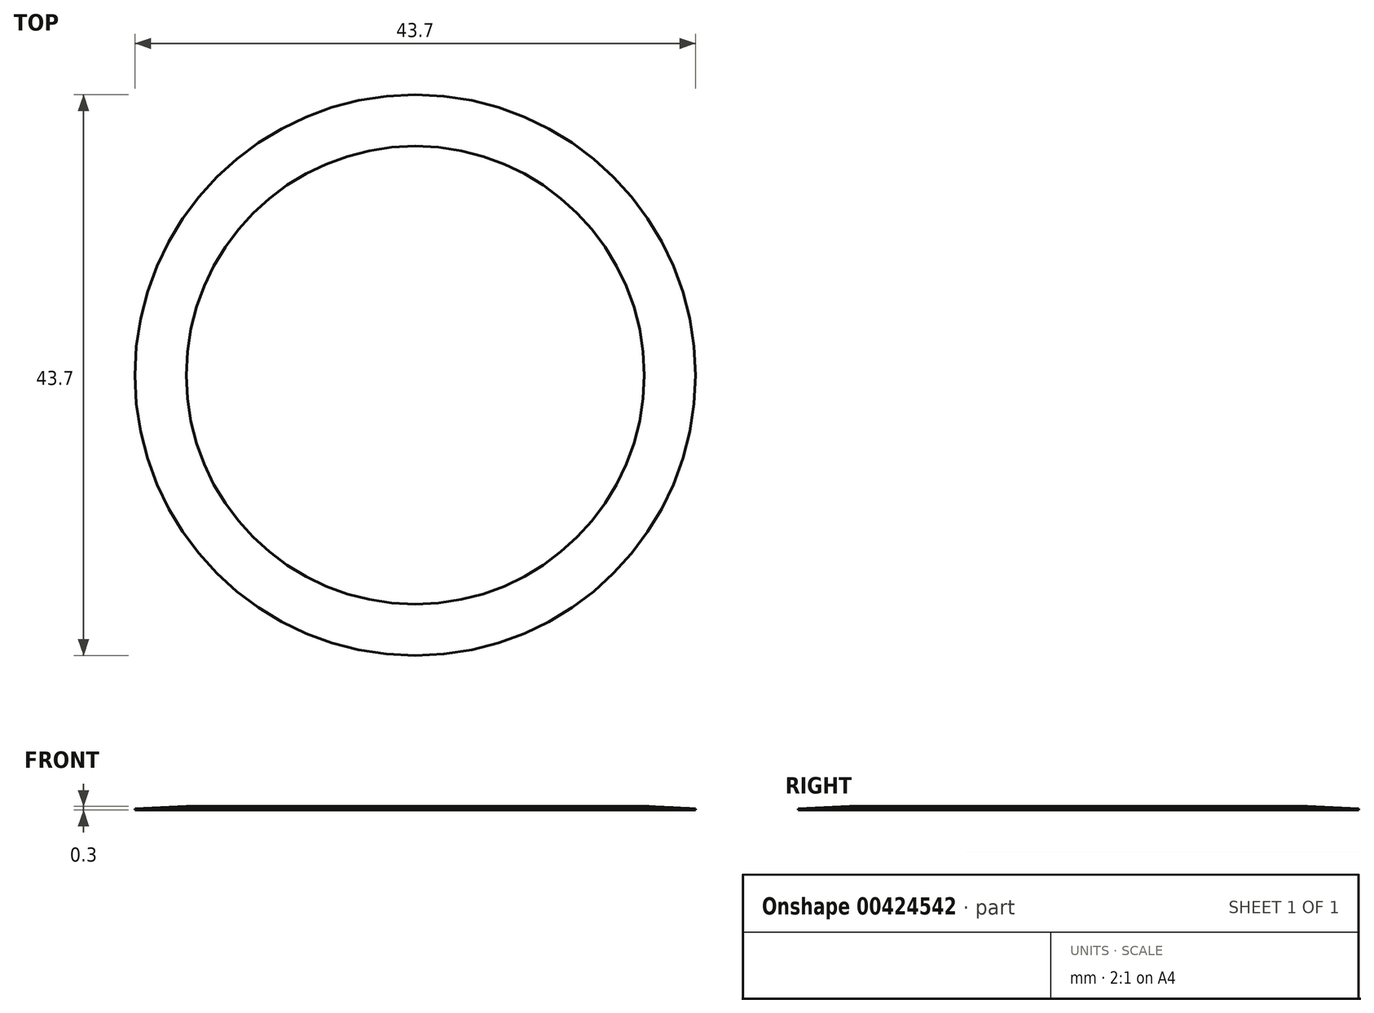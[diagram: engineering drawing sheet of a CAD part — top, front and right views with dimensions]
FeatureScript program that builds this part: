
annotation { "Feature Type Name" : "Feature", "Feature Type Description" : "" }
export const myFeature = defineFeature(function(context is Context, id is Id, definition is map)
    precondition{}
    {
        {
            var Q0;
            Q0=qCreatedBy(makeId("Top.planeOp"),FACE);
            var sketch = newSketch(context, id + "F0", { "sketchPlane" : qUnion([Q0])});
            skCircle(sketch, "E0", {"center": v(0, 0) * mm, "radius": 21.85 * mm});
            skSolve(sketch);
        }
        {
            var Q0;
            Q0=makeQuery(id+"F0.imprint","IMPRINT",FACE,{"disambiguationData":[TD([[makeQuery(id+"F0.imprint","IMPRINT",EDGE,{"derivedFrom":sQuery(id+"F0.wireOp",EDGE,"E0")}),1.0]])]});
            extrude(context, id + "F1", {"entities" : qUnion([Q0]), "depth" : .3 * mm});
        }
        {
            var Q0;
            Q0=makeQuery(id+"F1.opExtrude","CAP_EDGE",EDGE,{"disambiguationData":[OSD([sQuery(id+"F0.wireOp",EDGE,"E0")])],"isStart":false});
            chamfer(context, id + "F2", {"entities" : qUnion([Q0]), "chamferType" : ChamferType.TWO_OFFSETS, "width1" : .2 * mm, "oppositeDirection" : true, "width2" : 4 * mm, "tangentPropagation" : true});
        }
    });
